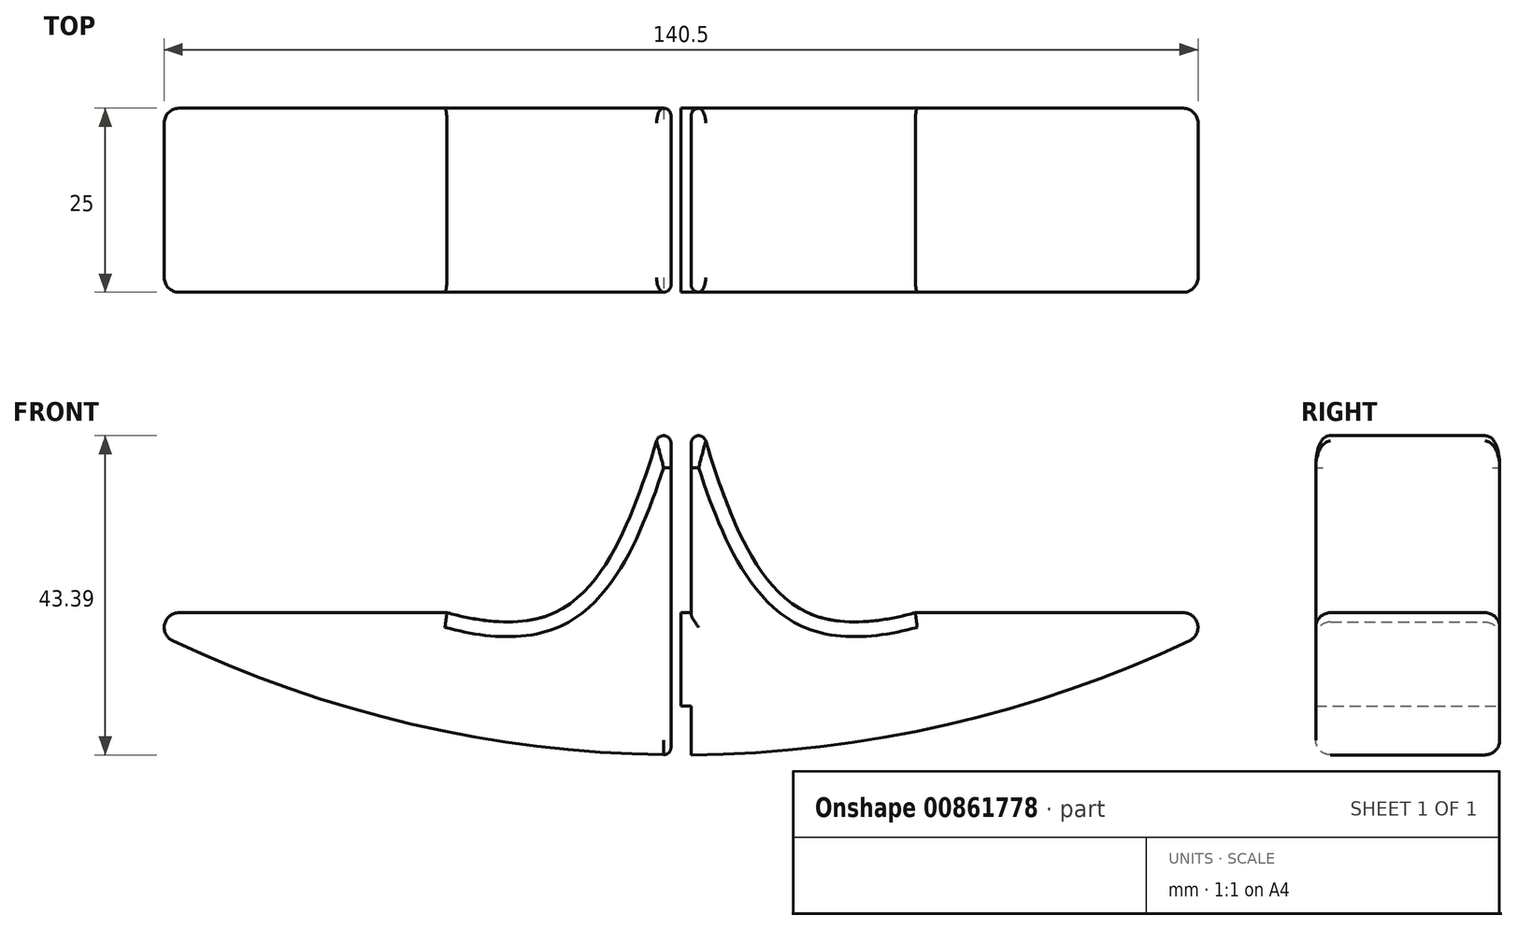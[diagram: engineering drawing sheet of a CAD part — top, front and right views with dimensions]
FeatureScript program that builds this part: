
annotation { "Feature Type Name" : "Feature", "Feature Type Description" : "" }
export const myFeature = defineFeature(function(context is Context, id is Id, definition is map)
    precondition{}
    {
        {
            var Q0;
            Q0=qCreatedBy(makeId("Front.planeOp"),FACE);
            var sketch = newSketch(context, id + "F0", { "sketchPlane" : qUnion([Q0])});
            skLineSegment(sketch, "E0", {"start": v(-76.64, 0) * mm, "end": v(0, 0) * mm});
            skLineSegment(sketch, "E1.0", {"start": v(-1.38, -12.7) * mm, "end": v(-1.38, -19.33) * mm});
            skLineSegment(sketch, "E2.0", {"start": v(1.38, -40.87) * mm, "end": v(1.38, -40.88) * mm});
            skArc(sketch, "E3", {"start": v(-76.64, 0) * mm, "mid": v(-40.19, -14.25) * mm, "end": v(-1.38, -19.33) * mm});
            skLineSegment(sketch, "E4.trimOffspring", {"start": v(-1.38, -40.87) * mm, "end": v(-1.38, -40.88) * mm});
            skLineSegment(sketch, "E5", {"start": v(0, -12.7) * mm, "end": v(-1.38, -12.7) * mm});
            skPoint(sketch, "E6.orphan", {"position": v(1.38, -19.33) * mm});
            skPoint(sketch, "E7.end.orphan", {"position": v(0, -19.33) * mm});
            skPoint(sketch, "E7.start.orphan", {"position": v(-1.38, -19.33) * mm});
            skLineSegment(sketch, "E8.MirrorCS", {"start": v(0, -12.7) * mm, "end": v(1.38, -12.7) * mm});
            skLineSegment(sketch, "E9.MirrorCS", {"start": v(1.38, -12.7) * mm, "end": v(1.38, -19.33) * mm});
            skLineSegment(sketch, "E10.MirrorCS", {"start": v(76.64, 0) * mm, "end": v(0, 0) * mm});
            skArc(sketch, "E11.MirrorCS", {"start": v(76.64, 0) * mm, "mid": v(40.19, -14.25) * mm, "end": v(1.38, -19.33) * mm});
            skPoint(sketch, "E12.orphan", {"position": v(1.38, 0) * mm});
            skPoint(sketch, "E13.orphan", {"position": v(-1.38, 0) * mm});
            skLineSegment(sketch, "E14", {"start": v(-1.38, 0) * mm, "end": v(1.38, 0) * mm});
            skLineSegment(sketch, "E15", {"start": v(1.38, 0) * mm, "end": v(-1.38, 0) * mm});
            skLineSegment(sketch, "E16", {"start": v(0, 0) * mm, "end": v(0, -12.7) * mm});
            skLineSegment(sketch, "E17", {"start": v(0, -12.7) * mm, "end": v(0, 0) * mm});
            skLineSegment(sketch, "E18", {"start": v(1.38, 0) * mm, "end": v(1.38, -12.7) * mm});
            skLineSegment(sketch, "E19", {"start": v(-1.38, 0) * mm, "end": v(-1.38, -12.7) * mm});
            skLineSegment(sketch, "E20", {"start": v(-1.38, -12.7) * mm, "end": v(0, -12.7) * mm});
            skLineSegment(sketch, "E21", {"start": v(-1.38, 0) * mm, "end": v(-1.38, 30) * mm});
            skLineSegment(sketch, "E22", {"start": v(1.38, 0) * mm, "end": v(1.38, 30) * mm});
            skLineSegment(sketch, "E23", {"start": v(-1.38, 30) * mm, "end": v(1.38, 30) * mm});
            skFitSpline(sketch, "E24", {"points": [v(1.38, 30) * mm, v(17.2, 0) * mm, v(51.87, 7.84) * mm], "startDerivative": vector(22.99, -79.55) * mm, "endDerivative": vector(77.78, 34.78) * mm});
            skFitSpline(sketch, "E25.MirrorCS", {"points": [v(-1.38, 30) * mm, v(-17.2, 0) * mm, v(-51.87, 7.84) * mm], "startDerivative": vector(-22.99, -79.55) * mm, "endDerivative": vector(-77.78, 34.78) * mm});
            skSolve(sketch);
        }
        {
            var Q0;
            {var subQ0=sQuery(id+"F0.wireOp",EDGE,"E21");Q0=makeQuery(id+"F0.imprint","IMPRINT",FACE,{"disambiguationData":[TD([[makeQuery(id+"F0.imprint","IMPRINT",EDGE,{"derivedFrom":subQ0}),1.0]])]});}
            var Q1;
            Q1=makeQuery(id+"F0.imprint","IMPRINT",FACE,{"disambiguationData":[TD([[makeQuery(id+"F0.imprint","IMPRINT",EDGE,{"derivedFrom":sQuery(id+"F0.wireOp",EDGE,"E1.0")}),-1.0]])]});
            var Q2;
            {var subQ1=sQuery(id+"F0.wireOp",EDGE,"E15");Q2=makeQuery(id+"F0.imprint","IMPRINT",FACE,{"disambiguationData":[TD([[makeQuery(id+"F0.imprint","IMPRINT",EDGE,{"derivedFrom":subQ1}),-1.0]])]});}
            var Q3;
            Q3=makeQuery(id+"F0.imprint","IMPRINT",FACE,{"disambiguationData":[TD([[makeQuery(id+"F0.imprint","IMPRINT",EDGE,{"derivedFrom":sQuery(id+"F0.wireOp",EDGE,"E8.MirrorCS")}),1.0]])]});
            var Q4;
            {var subQ0=sQuery(id+"F0.wireOp",EDGE,"E22");Q4=makeQuery(id+"F0.imprint","IMPRINT",FACE,{"disambiguationData":[TD([[makeQuery(id+"F0.imprint","IMPRINT",EDGE,{"derivedFrom":subQ0}),-1.0]])]});}
            var Q5;
            {var subQ0=sQuery(id+"F0.wireOp",EDGE,"E17");Q5=makeQuery(id+"F0.imprint","IMPRINT",FACE,{"disambiguationData":[TD([[makeQuery(id+"F0.imprint","IMPRINT",EDGE,{"derivedFrom":subQ0}),1.0]])]});}
            var Q6;
            Q6=makeQuery(id+"F0.imprint","IMPRINT",FACE,{"disambiguationData":[TD([[makeQuery(id+"F0.imprint","IMPRINT",EDGE,{"derivedFrom":sQuery(id+"F0.wireOp",EDGE,"E9.MirrorCS")}),1.0]])]});
            extrude(context, id + "F1", {"entities" : qUnion([Q0, Q1, Q2, Q3, Q4, Q5, Q6]), "endBound" : BoundingType.SYMMETRIC, "depth" : 25 * mm, "offsetDistance" : 25 * mm});
        }
        {
            var Q0;
            Q0=makeQuery(id+"F1.opExtrude","SWEPT_EDGE",EDGE,{"disambiguationData":[OSD([sQuery(id+"F0.wireOp",EDGE,"E10.MirrorCS"),sQuery(id+"F0.wireOp",EDGE,"E11.MirrorCS")])]});
            var Q1;
            Q1=makeQuery(id+"F1.opExtrude","SWEPT_EDGE",EDGE,{"disambiguationData":[OSD([sQuery(id+"F0.wireOp",EDGE,"E3"),sQuery(id+"F0.wireOp",EDGE,"E0")])]});
            fillet(context, id + "F2", {"entities" : qUnion([Q0, Q1]), "radius" : 2 * mm, "tangentPropagation" : true, "allowEdgeOverflow" : false});
        }
        {
            var Q0;
            Q0=makeQuery(id+"F1.opExtrude","CAP_EDGE",EDGE,{"disambiguationData":[OSD([sQuery(id+"F0.wireOp",EDGE,"E0")])],"isStart":false});
            var Q1;
            Q1=makeQuery(id+"F1.opExtrude","CAP_EDGE",EDGE,{"disambiguationData":[OSD([sQuery(id+"F0.wireOp",EDGE,"E25.MirrorCS")])],"isStart":false});
            var Q2;
            Q2=makeQuery(id+"F1.opExtrude","CAP_EDGE",EDGE,{"disambiguationData":[OSD([sQuery(id+"F0.wireOp",EDGE,"E24")])],"isStart":false});
            var Q3;
            Q3=makeQuery(id+"F1.opExtrude","CAP_EDGE",EDGE,{"disambiguationData":[OSD([sQuery(id+"F0.wireOp",EDGE,"E10.MirrorCS")])],"isStart":false});
            var Q4;
            Q4=makeQuery(id+"F1.opExtrude","CAP_EDGE",EDGE,{"disambiguationData":[OSD([sQuery(id+"F0.wireOp",EDGE,"E23")])],"isStart":false});
            fillet(context, id + "F3", {"entities" : qUnion([Q0, Q1, Q2, Q3, Q4]), "radius" : 2 * mm, "tangentPropagation" : true, "allowEdgeOverflow" : false});
        }
        {
            var Q0;
            Q0=makeQuery(id+"F1.opExtrude","CAP_EDGE",EDGE,{"disambiguationData":[OSD([sQuery(id+"F0.wireOp",EDGE,"E0")])],"isStart":true});
            var Q1;
            Q1=makeQuery(id+"F1.opExtrude","CAP_EDGE",EDGE,{"disambiguationData":[OSD([sQuery(id+"F0.wireOp",EDGE,"E25.MirrorCS")])],"isStart":true});
            var Q2;
            Q2=makeQuery(id+"F1.opExtrude","CAP_EDGE",EDGE,{"disambiguationData":[OSD([sQuery(id+"F0.wireOp",EDGE,"E23")])],"isStart":true});
            var Q3;
            Q3=makeQuery(id+"F1.opExtrude","CAP_EDGE",EDGE,{"disambiguationData":[OSD([sQuery(id+"F0.wireOp",EDGE,"E24")])],"isStart":true});
            var Q4;
            Q4=makeQuery(id+"F1.opExtrude","CAP_EDGE",EDGE,{"disambiguationData":[OSD([sQuery(id+"F0.wireOp",EDGE,"E10.MirrorCS")])],"isStart":true});
            fillet(context, id + "F4", {"entities" : qUnion([Q0, Q1, Q2, Q3, Q4]), "radius" : 2 * mm, "tangentPropagation" : true, "allowEdgeOverflow" : false});
        }
        {
            var Q0;
            Q0=makeQuery(id+"F1.opExtrude","SWEPT_EDGE",EDGE,{"disambiguationData":[OSD([sQuery(id+"F0.wireOp",EDGE,"E22"),sQuery(id+"F0.wireOp",EDGE,"E23"),sQuery(id+"F0.wireOp",EDGE,"E24")])]});
            var Q1;
            Q1=makeQuery(id+"F1.opExtrude","SWEPT_EDGE",EDGE,{"disambiguationData":[OSD([sQuery(id+"F0.wireOp",EDGE,"E21"),sQuery(id+"F0.wireOp",EDGE,"E23"),sQuery(id+"F0.wireOp",EDGE,"E25.MirrorCS")])]});
            var Q2;
            Q2=makeQuery(id+"F3.opFillet","BLEND_EDGE",EDGE,{"blendedFrom":[makeQuery(id+"F1.opExtrude","CAP_EDGE",EDGE,{"disambiguationData":[OSD([sQuery(id+"F0.wireOp",EDGE,"E24")])],"isStart":false}),makeQuery(id+"F1.opExtrude","SWEPT_FACE",FACE,{"disambiguationData":[OSD([sQuery(id+"F0.wireOp",EDGE,"E23")])]})],"blendedInto":[makeQuery(id+"F1.opExtrude","SWEPT_FACE",FACE,{"disambiguationData":[OSD([sQuery(id+"F0.wireOp",EDGE,"E23")])]})]});
            fillet(context, id + "F5", {"entities" : qUnion([Q0, Q1, Q2]), "radius" : 1 * mm, "tangentPropagation" : true, "allowEdgeOverflow" : false});
        }
    });
